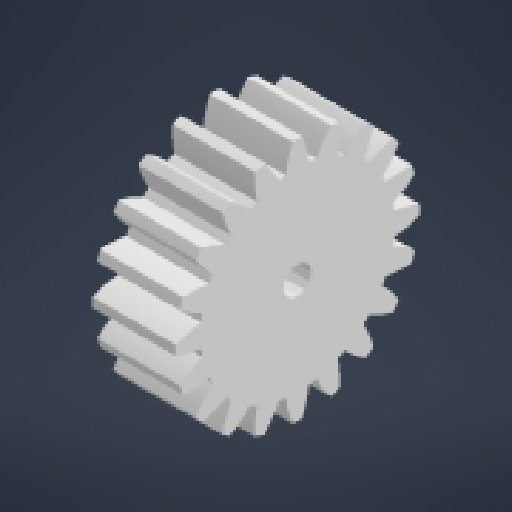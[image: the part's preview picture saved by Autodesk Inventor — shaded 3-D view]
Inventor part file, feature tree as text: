
AUTODESK INVENTOR PART (.ipt)
format: ipt  version: 2024 (Build 280153000, 153)  size: 236,032 bytes
history: native  units: mm
features: other x4, extrude x1, sketch x1
ambient origin geometry x8: Origin, YZ Plane, XZ Plane, XY Plane, X Axis, Y Axis, Z Axis, Center Point
bodies: Body1 (feature_tree)
feature tree (6):
  other  "{BB8FE430-83BF-418D-8DF9-9B323D3DB9B9}"
  other  "솔리드1"
  extrude  "돌출1"  Depth=44.31mm
  other  "스퍼 기어 톱니1"
  sketch  "스케치1"
  other  "스퍼 기어1"
